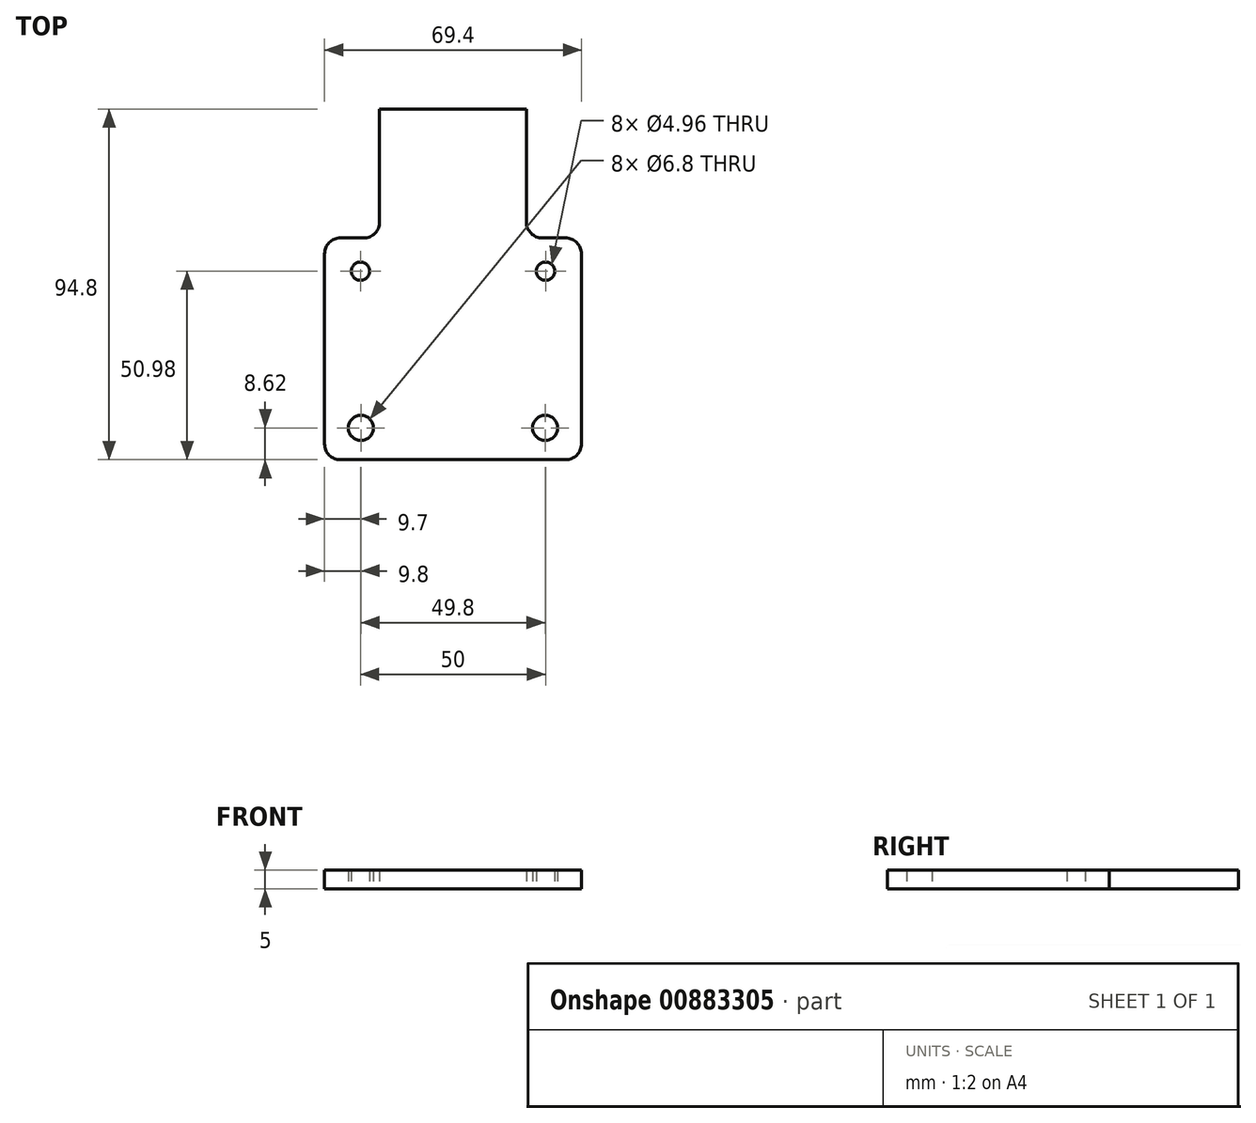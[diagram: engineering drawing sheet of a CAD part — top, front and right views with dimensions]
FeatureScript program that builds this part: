
annotation { "Feature Type Name" : "Feature", "Feature Type Description" : "" }
export const myFeature = defineFeature(function(context is Context, id is Id, definition is map)
    precondition{}
    {
        {
            var Q0;
            Q0=qCreatedBy(makeId("Top.planeOp"),FACE);
            var sketch = newSketch(context, id + "F0", { "sketchPlane" : qUnion([Q0])});
            skLineSegment(sketch, "E0.bottom", {"start": v(0, 0) * mm, "end": v(69.4, 0) * mm});
            skLineSegment(sketch, "E0.top", {"start": v(0, 59.96) * mm, "end": v(14.87, 59.96) * mm});
            skLineSegment(sketch, "E0.left", {"start": v(0, 0) * mm, "end": v(0, 59.96) * mm});
            skLineSegment(sketch, "E0.right", {"start": v(69.4, 0) * mm, "end": v(69.4, 59.96) * mm});
            skLineSegment(sketch, "E1.top", {"start": v(14.87, 94.8) * mm, "end": v(54.53, 94.8) * mm});
            skLineSegment(sketch, "E1.left", {"start": v(14.87, 59.96) * mm, "end": v(14.87, 94.8) * mm});
            skLineSegment(sketch, "E1.right", {"start": v(54.53, 59.96) * mm, "end": v(54.53, 94.8) * mm});
            skLineSegment(sketch, "E2.trimOffspring", {"start": v(54.53, 59.96) * mm, "end": v(69.4, 59.96) * mm});
            skLineSegment(sketch, "E3", {"start": v(34.7, 94.8) * mm, "end": v(34.7, 0) * mm, "construction": true});
            skCircle(sketch, "E4", {"center": v(59.7, 50.98) * mm, "radius": 2.48 * mm});
            skCircle(sketch, "E5", {"center": v(59.6, 8.62) * mm, "radius": 3.4 * mm});
            skLineSegment(sketch, "E6", {"start": v(62.18, 50.98) * mm, "end": v(62.18, 40.26) * mm, "construction": true});
            skLineSegment(sketch, "E7", {"start": v(59.7, 53.46) * mm, "end": v(52.56, 53.46) * mm, "construction": true});
            skCircle(sketch, "E8.MirrorC", {"center": v(9.7, 50.98) * mm, "radius": 2.48 * mm});
            skPoint(sketch, "E9", {"position": v(63, 8.62) * mm});
            skPoint(sketch, "E10", {"position": v(59.6, 5.22) * mm});
            skCircle(sketch, "E11.MirrorC", {"center": v(9.8, 8.62) * mm, "radius": 3.4 * mm});
            skSolve(sketch);
        }
        {
            var Q0;
            Q0 = qSketchRegion(id + "F0", true);
            extrude(context, id + "F1", {"entities" : qUnion([Q0]), "depth" : 5 * mm, "offsetDistance" : 25.4 * mm});
        }
        {
            var Q0;
            Q0=makeQuery(id+"F1.opExtrude","SWEPT_EDGE",EDGE,{"disambiguationData":[OSD([sQuery(id+"F0.wireOp",EDGE,"E1.right"),sQuery(id+"F0.wireOp",EDGE,"E2.trimOffspring")])]});
            var Q1;
            Q1=makeQuery(id+"F1.opExtrude","SWEPT_EDGE",EDGE,{"disambiguationData":[OSD([sQuery(id+"F0.wireOp",EDGE,"E0.top"),sQuery(id+"F0.wireOp",EDGE,"E1.left")])]});
            var Q2;
            Q2=makeQuery(id+"F1.opExtrude","SWEPT_EDGE",EDGE,{"disambiguationData":[OSD([sQuery(id+"F0.wireOp",EDGE,"E0.top"),sQuery(id+"F0.wireOp",EDGE,"E0.left")])]});
            var Q3;
            Q3=makeQuery(id+"F1.opExtrude","SWEPT_EDGE",EDGE,{"disambiguationData":[OSD([sQuery(id+"F0.wireOp",EDGE,"E0.right"),sQuery(id+"F0.wireOp",EDGE,"E2.trimOffspring")])]});
            var Q4;
            Q4=makeQuery(id+"F1.opExtrude","SWEPT_EDGE",EDGE,{"disambiguationData":[OSD([sQuery(id+"F0.wireOp",EDGE,"E0.bottom"),sQuery(id+"F0.wireOp",EDGE,"E0.right")])]});
            var Q5;
            Q5=makeQuery(id+"F1.opExtrude","SWEPT_EDGE",EDGE,{"disambiguationData":[OSD([sQuery(id+"F0.wireOp",EDGE,"E0.bottom"),sQuery(id+"F0.wireOp",EDGE,"E0.left")])]});
            fillet(context, id + "F2", {"entities" : qUnion([Q0, Q1, Q2, Q3, Q4, Q5]), "radius" : 4.3 * mm, "tangentPropagation" : true, "allowEdgeOverflow" : false});
        }
    });
